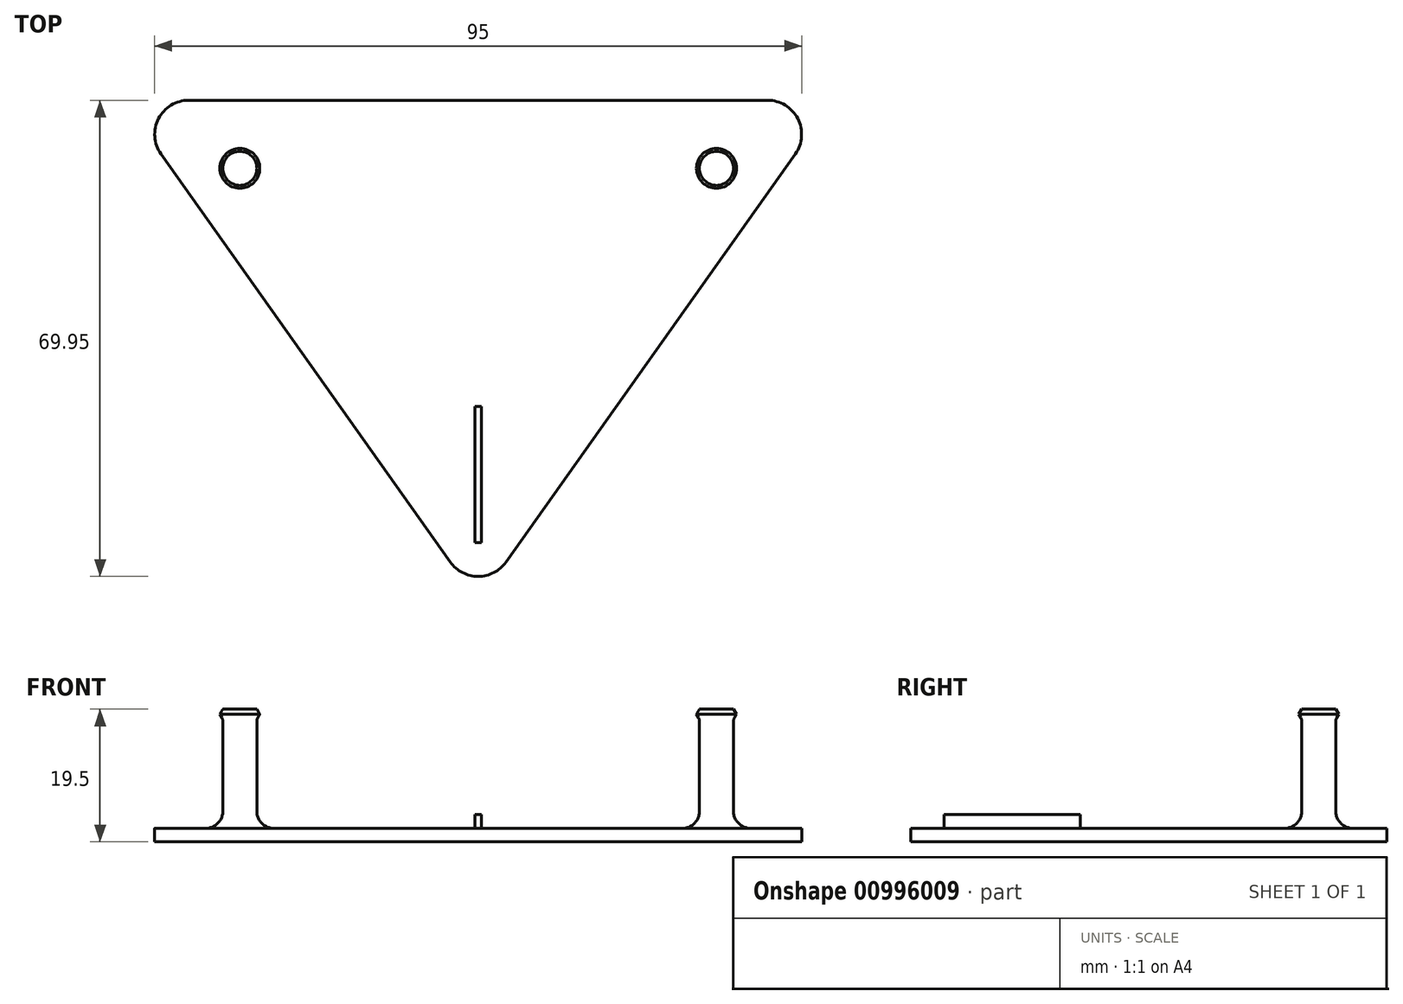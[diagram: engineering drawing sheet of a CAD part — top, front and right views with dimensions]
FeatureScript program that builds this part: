
annotation { "Feature Type Name" : "Feature", "Feature Type Description" : "" }
export const myFeature = defineFeature(function(context is Context, id is Id, definition is map)
    precondition{}
    {
        {
            var Q0;
            Q0=qCreatedBy(makeId("Top.planeOp"),FACE);
            var sketch = newSketch(context, id + "F0", { "sketchPlane" : qUnion([Q0])});
            skLineSegment(sketch, "E0", {"start": v(-35, 0) * mm, "end": v(35, 0) * mm, "construction": true});
            skLineSegment(sketch, "E1", {"start": v(0, 0) * mm, "end": v(0, -45) * mm, "construction": true});
            skLineSegment(sketch, "E2", {"start": v(-42.5, 10) * mm, "end": v(42.5, 10) * mm});
            skLineSegment(sketch, "E3", {"start": v(0, 0) * mm, "end": v(0, 75.2) * mm, "construction": true});
            skLineSegment(sketch, "E4", {"start": v(-46.58, 2.1) * mm, "end": v(-4.08, -57.84) * mm});
            skLineSegment(sketch, "E5", {"start": v(4.08, -57.84) * mm, "end": v(46.58, 2.1) * mm});
            skPoint(sketch, "E6.visualSharp", {"position": v(-52.17, 10) * mm});
            skArc(sketch, "E6.filletArc", {"start": v(-42.5, 10) * mm, "mid": v(-46.94, 7.3) * mm, "end": v(-46.58, 2.1) * mm});
            skPoint(sketch, "E7.visualSharp", {"position": v(0, -63.6) * mm});
            skArc(sketch, "E7.filletArc", {"start": v(-4.08, -57.84) * mm, "mid": v(0, -59.95) * mm, "end": v(4.08, -57.84) * mm});
            skPoint(sketch, "E8.visualSharp", {"position": v(52.17, 10) * mm});
            skArc(sketch, "E8.filletArc", {"start": v(46.58, 2.1) * mm, "mid": v(46.94, 7.3) * mm, "end": v(42.5, 10) * mm});
            skPoint(sketch, "E9", {"position": v(0, 10) * mm});
            skPoint(sketch, "E10", {"position": v(-35, 0) * mm});
            skPoint(sketch, "E11", {"position": v(35, 0) * mm});
            skPoint(sketch, "E12", {"position": v(0, -45) * mm});
            skSolve(sketch);
        }
        {
            var Q0;
            Q0 = qSketchRegion(id + "F0", true);
            extrude(context, id + "F1", {"entities" : qUnion([Q0]), "depth" : 2 * mm, "offsetDistance" : 25 * mm});
        }
        {
            var Q0;
            Q0=qCreatedBy(makeId("Top.planeOp"),FACE);
            var sketch = newSketch(context, id + "F2", { "sketchPlane" : qUnion([Q0])});
            skCircle(sketch, "E13", {"center": v(-35, 0) * mm, "radius": 2.5 * mm});
            skCircle(sketch, "E14", {"center": v(35, 0) * mm, "radius": 2.5 * mm});
            skSolve(sketch);
        }
        {
            var Q0;
            Q0 = qSketchRegion(id + "F2", true);
            extrude(context, id + "F3", {"entities" : qUnion([Q0]), "operationType" : NewBodyOperationType.ADD, "depth" : 18 * mm, "offsetDistance" : 25 * mm});
        }
        {
            var Q0;
            Q0=makeQuery(id+"F1.opExtrude","CAP_FACE",FACE,{"disambiguationData":[OSD([sQuery(id+"F0.wireOp",EDGE,"E2"),sQuery(id+"F0.wireOp",EDGE,"E4"),sQuery(id+"F0.wireOp",EDGE,"E5"),sQuery(id+"F0.wireOp",EDGE,"E6.filletArc"),sQuery(id+"F0.wireOp",EDGE,"E7.filletArc"),sQuery(id+"F0.wireOp",EDGE,"E8.filletArc")])],"isStart":false});
            var sketch = newSketch(context, id + "F4", { "sketchPlane" : qUnion([Q0])});
            skLineSegment(sketch, "E15.bottom", {"start": v(-0.5, -35) * mm, "end": v(0.5, -35) * mm});
            skLineSegment(sketch, "E15.top", {"start": v(-0.5, -55) * mm, "end": v(0.5, -55) * mm});
            skLineSegment(sketch, "E15.left", {"start": v(-0.5, -35) * mm, "end": v(-0.5, -55) * mm});
            skLineSegment(sketch, "E15.right", {"start": v(0.5, -35) * mm, "end": v(0.5, -55) * mm});
            skLineSegment(sketch, "E16", {"start": v(-8.92, -45) * mm, "end": v(6.79, -45) * mm, "construction": true});
            skPoint(sketch, "E17", {"position": v(0.5, -45) * mm});
            skPoint(sketch, "E18", {"position": v(0, -35) * mm});
            skSolve(sketch);
        }
        {
            var Q0;
            Q0 = qSketchRegion(id + "F4", true);
            extrude(context, id + "F5", {"entities" : qUnion([Q0]), "operationType" : NewBodyOperationType.ADD, "depth" : 2 * mm, "offsetDistance" : 25 * mm});
        }
        {
            var Q0;
            Q0=makeQuery(id+"F3.boolean.opBoolean","INTERSECT",EDGE,{"derivedFrom":[makeQuery(id+"F1.opExtrude","CAP_FACE",FACE,{"disambiguationData":[OSD([sQuery(id+"F0.wireOp",EDGE,"E2"),sQuery(id+"F0.wireOp",EDGE,"E4"),sQuery(id+"F0.wireOp",EDGE,"E5"),sQuery(id+"F0.wireOp",EDGE,"E6.filletArc"),sQuery(id+"F0.wireOp",EDGE,"E7.filletArc"),sQuery(id+"F0.wireOp",EDGE,"E8.filletArc")])],"isStart":false}),makeQuery(id+"F3.opExtrude","SWEPT_FACE",FACE,{"disambiguationData":[OSD([sQuery(id+"F2.wireOp",EDGE,"E13")])]})]});
            var Q1;
            Q1=makeQuery(id+"F3.boolean.opBoolean","INTERSECT",EDGE,{"derivedFrom":[makeQuery(id+"F1.opExtrude","CAP_FACE",FACE,{"disambiguationData":[OSD([sQuery(id+"F0.wireOp",EDGE,"E2"),sQuery(id+"F0.wireOp",EDGE,"E4"),sQuery(id+"F0.wireOp",EDGE,"E5"),sQuery(id+"F0.wireOp",EDGE,"E6.filletArc"),sQuery(id+"F0.wireOp",EDGE,"E7.filletArc"),sQuery(id+"F0.wireOp",EDGE,"E8.filletArc")])],"isStart":false}),makeQuery(id+"F3.opExtrude","SWEPT_FACE",FACE,{"disambiguationData":[OSD([sQuery(id+"F2.wireOp",EDGE,"E14")])]})]});
            fillet(context, id + "F6", {"entities" : qUnion([Q0, Q1]), "radius" : 2.5 * mm, "tangentPropagation" : true, "allowEdgeOverflow" : false});
        }
        {
            var Q0;
            Q0=makeQuery(id+"F1.opExtrude","CAP_FACE",FACE,{"disambiguationData":[OSD([sQuery(id+"F0.wireOp",EDGE,"E2"),sQuery(id+"F0.wireOp",EDGE,"E4"),sQuery(id+"F0.wireOp",EDGE,"E5"),sQuery(id+"F0.wireOp",EDGE,"E6.filletArc"),sQuery(id+"F0.wireOp",EDGE,"E7.filletArc"),sQuery(id+"F0.wireOp",EDGE,"E8.filletArc")])],"isStart":false});
            var sketch = newSketch(context, id + "F7", { "sketchPlane" : qUnion([Q0])});
            skArc(sketch, "E19", {"start": v(4.5, 0) * mm, "mid": v(0, 4.5) * mm, "end": v(-4.5, 0) * mm});
            skArc(sketch, "E20", {"start": v(-4.5, -1.5) * mm, "mid": v(0, -15) * mm, "end": v(4.5, -1.5) * mm});
            skLineSegment(sketch, "E21", {"start": v(-4.5, 0) * mm, "end": v(-4.5, -1.5) * mm});
            skLineSegment(sketch, "E22", {"start": v(4.5, 0) * mm, "end": v(4.5, -1.5) * mm});
            skSolve(sketch);
        }
        {
            var Q0;
            Q0=makeQuery(id+"F3.opExtrude","CAP_FACE",FACE,{"disambiguationData":[OSD([sQuery(id+"F2.wireOp",EDGE,"E13")])],"isStart":false});
            cPlane(context, id + "F8", {"entities" : qUnion([Q0]), "cplaneType" : CPlaneType.OFFSET, "offset" : 0 * mm, "width" : 150 * mm, "height" : 150 * mm});
        }
        {
            var Q0;
            Q0=qCreatedBy(makeId("Front.planeOp"),FACE);
            var sketch = newSketch(context, id + "F9", { "sketchPlane" : qUnion([Q0])});
            skLineSegment(sketch, "E23", {"start": v(-28.38, 18) * mm, "end": v(-41.95, 18) * mm, "construction": true});
            skLineSegment(sketch, "E24", {"start": v(-35, 24.97) * mm, "end": v(-35, 0) * mm, "construction": true});
            skLineSegment(sketch, "E25", {"start": v(-35, 18) * mm, "end": v(-32.5, 18) * mm});
            skLineSegment(sketch, "E26", {"start": v(-32.5, 18) * mm, "end": v(-31.63, 19.5) * mm});
            skLineSegment(sketch, "E27", {"start": v(-31.63, 19.5) * mm, "end": v(-35, 19.5) * mm});
            skLineSegment(sketch, "E28", {"start": v(-35, 19.5) * mm, "end": v(-35, 18) * mm});
            skSolve(sketch);
        }
        {
            var Q0;
            Q0 = qSketchRegion(id + "F9", true);
            var Q1;
            Q1=sQuery(id+"F9.wireOp",EDGE,"E28");
            revolve(context, id + "F10", {"operationType" : NewBodyOperationType.ADD, "surfaceOperationType" : NewSurfaceOperationType.NEW, "entities" : qUnion([Q0]), "axis" : qUnion([Q1]), "revolveType" : RevolveType.FULL});
        }
        {
            var Q0;
            Q0=qCreatedBy(makeId("Front.planeOp"),FACE);
            var sketch = newSketch(context, id + "F11", { "sketchPlane" : qUnion([Q0])});
            skLineSegment(sketch, "E29", {"start": v(41.62, 18) * mm, "end": v(28.05, 18) * mm, "construction": true});
            skLineSegment(sketch, "E30", {"start": v(35, 24.97) * mm, "end": v(35, 0) * mm, "construction": true});
            skLineSegment(sketch, "E31", {"start": v(35, 18) * mm, "end": v(37.5, 18) * mm});
            skLineSegment(sketch, "E32", {"start": v(37.5, 18) * mm, "end": v(38.37, 19.5) * mm});
            skLineSegment(sketch, "E33", {"start": v(38.37, 19.5) * mm, "end": v(35, 19.5) * mm});
            skLineSegment(sketch, "E34", {"start": v(35, 19.5) * mm, "end": v(35, 18) * mm});
            skSolve(sketch);
        }
        {
            var Q0;
            Q0 = qSketchRegion(id + "F11", true);
            var Q1;
            Q1=sQuery(id+"F11.wireOp",EDGE,"E30");
            revolve(context, id + "F12", {"operationType" : NewBodyOperationType.ADD, "surfaceOperationType" : NewSurfaceOperationType.NEW, "entities" : qUnion([Q0]), "axis" : qUnion([Q1]), "revolveType" : RevolveType.FULL});
        }
        {
            var Q0;
            Q0=makeQuery(id+"F10.boolean.opBoolean","MERGE",EDGE,{"derivedFrom":[makeQuery(id+"F3.opExtrude","CAP_EDGE",EDGE,{"disambiguationData":[OSD([sQuery(id+"F2.wireOp",EDGE,"E13")])],"isStart":false}),makeQuery(id+"F10.opRevolve","SWEPT_EDGE",EDGE,{"disambiguationData":[OSD([sQuery(id+"F9.wireOp",EDGE,"E25"),sQuery(id+"F9.wireOp",EDGE,"E26")])]})]});
            var Q1;
            Q1=makeQuery(id+"F12.boolean.opBoolean","MERGE",EDGE,{"derivedFrom":[makeQuery(id+"F3.opExtrude","CAP_EDGE",EDGE,{"disambiguationData":[OSD([sQuery(id+"F2.wireOp",EDGE,"E14")])],"isStart":false}),makeQuery(id+"F12.opRevolve","SWEPT_EDGE",EDGE,{"disambiguationData":[OSD([sQuery(id+"F11.wireOp",EDGE,"E31"),sQuery(id+"F11.wireOp",EDGE,"E32")])]})]});
            fillet(context, id + "F13", {"entities" : qUnion([Q0, Q1]), "radius" : 1 * mm, "tangentPropagation" : true, "allowEdgeOverflow" : false});
        }
        {
            var Q0;
            Q0=makeQuery(id+"F10.opRevolve","SWEPT_EDGE",EDGE,{"disambiguationData":[OSD([sQuery(id+"F9.wireOp",EDGE,"E26"),sQuery(id+"F9.wireOp",EDGE,"E27")])]});
            var Q1;
            Q1=makeQuery(id+"F12.opRevolve","SWEPT_EDGE",EDGE,{"disambiguationData":[OSD([sQuery(id+"F11.wireOp",EDGE,"E32"),sQuery(id+"F11.wireOp",EDGE,"E33")])]});
            chamfer(context, id + "F14", {"entities" : qUnion([Q0, Q1]), "width" : .5 * mm, "tangentPropagation" : true});
        }
    });
